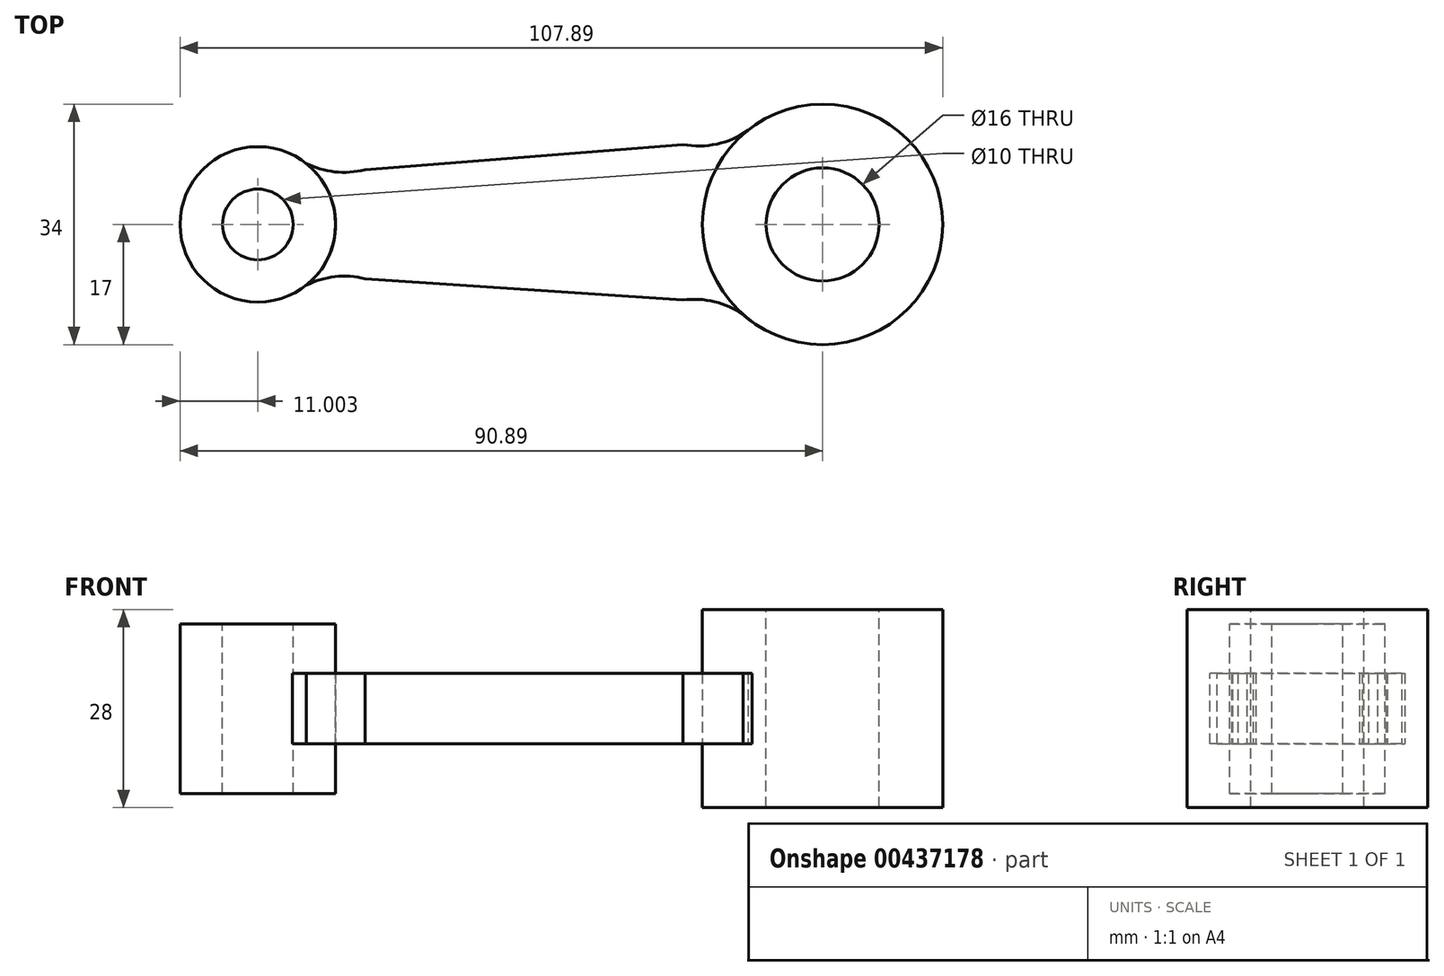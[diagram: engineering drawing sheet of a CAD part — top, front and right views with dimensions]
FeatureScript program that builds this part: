
annotation { "Feature Type Name" : "Feature", "Feature Type Description" : "" }
export const myFeature = defineFeature(function(context is Context, id is Id, definition is map)
    precondition{}
    {
        {
            var Q0;
            Q0=qCreatedBy(makeId("Top.planeOp"),FACE);
            var sketch = newSketch(context, id + "F0", { "sketchPlane" : qUnion([Q0])});
            skCircle(sketch, "E0", {"center": v(0, 0) * mm, "radius": 17 * mm});
            skCircle(sketch, "E1", {"center": v(0, 0) * mm, "radius": 8 * mm});
            skSolve(sketch);
        }
        {
            var Q0;
            Q0 = qSketchRegion(id + "F0", true);
            extrude(context, id + "F1", {"entities" : qUnion([Q0]), "oppositeDirection" : true, "depth" : 14 * mm});
        }
        {
            var Q0;
            Q0=makeQuery(id+"F1.opExtrude","CAP_FACE",FACE,{"disambiguationData":[OSD([sQuery(id+"F0.wireOp",EDGE,"E0"),sQuery(id+"F0.wireOp",EDGE,"E1")])],"isStart":true});
            var sketch = newSketch(context, id + "F2", { "sketchPlane" : qUnion([Q0])});
            skCircle(sketch, "E2", {"center": v(0, 0) * mm, "radius": 8 * mm});
            skCircle(sketch, "E3", {"center": v(0, 0) * mm, "radius": 17 * mm});
            skSolve(sketch);
        }
        {
            var Q0;
            Q0 = qSketchRegion(id + "F2", true);
            extrude(context, id + "F3", {"entities" : qUnion([Q0]), "operationType" : NewBodyOperationType.ADD, "depth" : 14 * mm});
        }
        {
            var Q0;
            Q0=qCreatedBy(makeId("Top.planeOp"),FACE);
            var sketch = newSketch(context, id + "F4", { "sketchPlane" : qUnion([Q0])});
            skCircle(sketch, "E4", {"center": v(-79.89, 0) * mm, "radius": 5 * mm});
            skCircle(sketch, "E5", {"center": v(-79.89, 0) * mm, "radius": 11 * mm});
            skSolve(sketch);
        }
        {
            var Q0;
            Q0 = qSketchRegion(id + "F4", true);
            extrude(context, id + "F5", {"entities" : qUnion([Q0]), "oppositeDirection" : true, "depth" : 12 * mm});
        }
        {
            var Q0;
            Q0=qCreatedBy(makeId("Top.planeOp"),FACE);
            var sketch = newSketch(context, id + "F6", { "sketchPlane" : qUnion([Q0])});
            skCircle(sketch, "E6", {"center": v(-79.89, 0) * mm, "radius": 5 * mm});
            skCircle(sketch, "E7", {"center": v(-79.89, 0) * mm, "radius": 11 * mm});
            skSolve(sketch);
        }
        {
            var Q0;
            Q0 = qSketchRegion(id + "F6", true);
            extrude(context, id + "F7", {"entities" : qUnion([Q0]), "operationType" : NewBodyOperationType.ADD, "depth" : 12 * mm});
        }
        {
            var Q0;
            Q0=qCreatedBy(makeId("Top.planeOp"),FACE);
            var sketch = newSketch(context, id + "F8", { "sketchPlane" : qUnion([Q0])});
            skPoint(sketch, "E8", {"position": v(0, 0) * mm});
            skLineSegment(sketch, "E9", {"start": v(-64.74, 7.74) * mm, "end": v(-19.74, 11.3) * mm});
            skLineSegment(sketch, "E10", {"start": v(-19.74, -10.7) * mm, "end": v(-64.74, -7.67) * mm});
            skPoint(sketch, "E11.orphan", {"position": v(-80, 0) * mm});
            skLineSegment(sketch, "E12", {"start": v(-13.5, 11.79) * mm, "end": v(-12.14, 11.9) * mm});
            skArc(sketch, "E13", {"start": v(-71.57, -7.2) * mm, "mid": v(-69.48, -3.56) * mm, "end": v(-68.9, 0.6) * mm});
            skArc(sketch, "E14", {"start": v(-12.14, 11.9) * mm, "mid": v(-17, 0.5) * mm, "end": v(-12.81, -11.17) * mm});
            skArc(sketch, "E15", {"start": v(-19.74, 11.3) * mm, "mid": v(-14.6, 11.46) * mm, "end": v(-9.98, 13.76) * mm});
            skPoint(sketch, "E16", {"position": v(-19.74, -10.7) * mm});
            skArc(sketch, "E17", {"start": v(-9.98, -13.76) * mm, "mid": v(-14.52, -11.14) * mm, "end": v(-19.74, -10.7) * mm});
            skArc(sketch, "E18", {"start": v(-9.98, 13.76) * mm, "mid": v(-17, 0) * mm, "end": v(-9.98, -13.76) * mm});
            skLineSegment(sketch, "E19", {"start": v(-79.89, 0) * mm, "end": v(-79.85, 0.08) * mm});
            skArc(sketch, "E20", {"start": v(-64.74, -7.67) * mm, "mid": v(-70.13, -7.58) * mm, "end": v(-75.03, -9.87) * mm});
            skPoint(sketch, "E21", {"position": v(-64.74, 7.74) * mm});
            skLineSegment(sketch, "E22", {"start": v(-79.85, 0.08) * mm, "end": v(-80, 0) * mm});
            skArc(sketch, "E23", {"start": v(-75.03, 9.87) * mm, "mid": v(-70.12, 7.62) * mm, "end": v(-64.74, 7.74) * mm});
            skArc(sketch, "E24.trimOffspring", {"start": v(-70.1, 5.02) * mm, "mid": v(-70.77, 6.16) * mm, "end": v(-71.57, 7.2) * mm});
            skArc(sketch, "E25", {"start": v(-75.03, -9.87) * mm, "mid": v(-68.89, 0) * mm, "end": v(-75.03, 9.87) * mm});
            skSolve(sketch);
        }
        {
            var Q0;
            Q0 = qSketchRegion(id + "F8", true);
            extrude(context, id + "F9", {"entities" : qUnion([Q0]), "endBound" : BoundingType.SYMMETRIC, "oppositeDirection" : true, "depth" : 10 * mm});
        }
        {
            var Q0;
            Q0 = qSketchRegion(id + "F8", true);
            extrude(context, id + "F10", {"entities" : qUnion([Q0]), "endBound" : BoundingType.SYMMETRIC, "depth" : 10 * mm});
        }
    });
